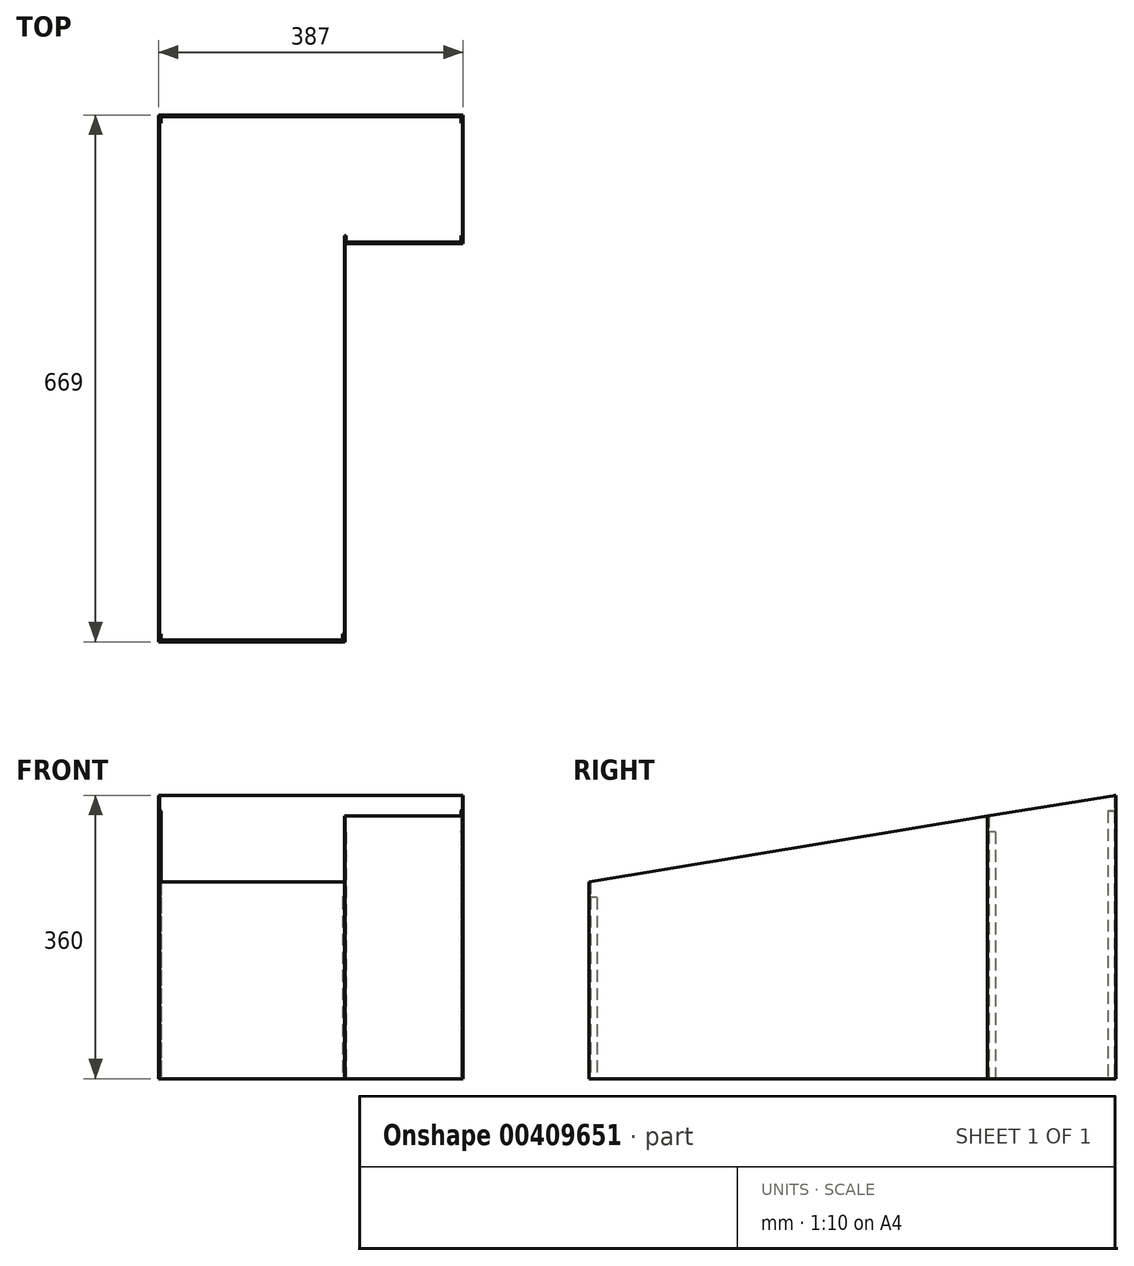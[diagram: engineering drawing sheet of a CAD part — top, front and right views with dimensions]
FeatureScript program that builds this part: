
annotation { "Feature Type Name" : "Feature", "Feature Type Description" : "" }
export const myFeature = defineFeature(function(context is Context, id is Id, definition is map)
    precondition{}
    {
        {
            var Q0;
            Q0=qCreatedBy(makeId("Top.planeOp"),FACE);
            var sketch = newSketch(context, id + "F0", { "sketchPlane" : qUnion([Q0])});
            skLineSegment(sketch, "E0.bottom", {"start": v(192.5, 300) * mm, "end": v(-192.5, 300) * mm});
            skLineSegment(sketch, "E0.top", {"start": v(192.5, 302) * mm, "end": v(-192.5, 302) * mm});
            skLineSegment(sketch, "E0.left", {"start": v(192.5, 300) * mm, "end": v(192.5, 302) * mm});
            skLineSegment(sketch, "E0.right", {"start": v(-192.5, 300) * mm, "end": v(-192.5, 302) * mm});
            skPoint(sketch, "E0.middle", {"position": v(0, 301) * mm});
            skLineSegment(sketch, "E1.bottom", {"start": v(-192.5, 300) * mm, "end": v(-190.5, 300) * mm});
            skLineSegment(sketch, "E1.top", {"start": v(-192.5, 292) * mm, "end": v(-190.5, 292) * mm});
            skLineSegment(sketch, "E1.left", {"start": v(-192.5, 300) * mm, "end": v(-192.5, 292) * mm});
            skLineSegment(sketch, "E1.right", {"start": v(-190.5, 300) * mm, "end": v(-190.5, 292) * mm});
            skLineSegment(sketch, "E2.bottom", {"start": v(192.5, 300) * mm, "end": v(190.5, 300) * mm});
            skLineSegment(sketch, "E2.top", {"start": v(192.5, 292) * mm, "end": v(190.5, 292) * mm});
            skLineSegment(sketch, "E2.left", {"start": v(192.5, 300) * mm, "end": v(192.5, 292) * mm});
            skLineSegment(sketch, "E2.right", {"start": v(190.5, 300) * mm, "end": v(190.5, 292) * mm});
            skSolve(sketch);
        }
        {
            var Q0;
            Q0 = qSketchRegion(id + "F0", true);
            extrude(context, id + "F1", {"entities" : qUnion([Q0]), "depth" : 360 * mm});
        }
        {
            var Q0;
            Q0=qCreatedBy(makeId("Top.planeOp"),FACE);
            var sketch = newSketch(context, id + "F2", { "sketchPlane" : qUnion([Q0])});
            skLineSegment(sketch, "E3.bottom", {"start": v(42.5, -367) * mm, "end": v(-192.5, -367) * mm});
            skLineSegment(sketch, "E3.top", {"start": v(42.5, -365) * mm, "end": v(-192.5, -365) * mm});
            skLineSegment(sketch, "E3.left", {"start": v(42.5, -367) * mm, "end": v(42.5, -365) * mm});
            skLineSegment(sketch, "E3.right", {"start": v(-192.5, -367) * mm, "end": v(-192.5, -365) * mm});
            skPoint(sketch, "E3.middle", {"position": v(-75, -366) * mm});
            skLineSegment(sketch, "E4.bottom", {"start": v(-192.5, -365) * mm, "end": v(-190.5, -365) * mm});
            skLineSegment(sketch, "E4.top", {"start": v(-192.5, -357) * mm, "end": v(-190.5, -357) * mm});
            skLineSegment(sketch, "E4.left", {"start": v(-192.5, -365) * mm, "end": v(-192.5, -357) * mm});
            skLineSegment(sketch, "E4.right", {"start": v(-190.5, -365) * mm, "end": v(-190.5, -357) * mm});
            skLineSegment(sketch, "E5.bottom", {"start": v(42.5, -365) * mm, "end": v(40.5, -365) * mm});
            skLineSegment(sketch, "E5.top", {"start": v(42.5, -357) * mm, "end": v(40.5, -357) * mm});
            skLineSegment(sketch, "E5.left", {"start": v(42.5, -365) * mm, "end": v(42.5, -357) * mm});
            skLineSegment(sketch, "E5.right", {"start": v(40.5, -365) * mm, "end": v(40.5, -357) * mm});
            skSolve(sketch);
        }
        {
            var Q0;
            Q0 = qSketchRegion(id + "F2", true);
            extrude(context, id + "F3", {"entities" : qUnion([Q0]), "depth" : 250 * mm});
        }
        {
            var Q0;
            Q0=qCreatedBy(makeId("Top.planeOp"),FACE);
            var sketch = newSketch(context, id + "F4", { "sketchPlane" : qUnion([Q0])});
            skLineSegment(sketch, "E6.bottom", {"start": v(192.5, 139) * mm, "end": v(42.5, 139) * mm});
            skLineSegment(sketch, "E6.top", {"start": v(192.5, 141) * mm, "end": v(42.5, 141) * mm});
            skLineSegment(sketch, "E6.left", {"start": v(192.5, 139) * mm, "end": v(192.5, 141) * mm});
            skLineSegment(sketch, "E6.right", {"start": v(42.5, 139) * mm, "end": v(42.5, 141) * mm});
            skPoint(sketch, "E6.middle", {"position": v(117.5, 140) * mm});
            skLineSegment(sketch, "E7.bottom", {"start": v(192.5, 141) * mm, "end": v(190.5, 141) * mm});
            skLineSegment(sketch, "E7.top", {"start": v(192.5, 149) * mm, "end": v(190.5, 149) * mm});
            skLineSegment(sketch, "E7.left", {"start": v(192.5, 141) * mm, "end": v(192.5, 149) * mm});
            skLineSegment(sketch, "E7.right", {"start": v(190.5, 141) * mm, "end": v(190.5, 149) * mm});
            skLineSegment(sketch, "E8.bottom", {"start": v(42.5, 141) * mm, "end": v(44.5, 141) * mm});
            skLineSegment(sketch, "E8.top", {"start": v(42.5, 149) * mm, "end": v(44.5, 149) * mm});
            skLineSegment(sketch, "E8.left", {"start": v(42.5, 141) * mm, "end": v(42.5, 149) * mm});
            skLineSegment(sketch, "E8.right", {"start": v(44.5, 141) * mm, "end": v(44.5, 149) * mm});
            skSolve(sketch);
        }
        {
            var Q0;
            Q0 = qSketchRegion(id + "F4", true);
            extrude(context, id + "F5", {"entities" : qUnion([Q0]), "depth" : 333.5 * mm});
        }
        {
            var Q0;
            Q0=qCreatedBy(makeId("Right.planeOp"),FACE);
            var sketch = newSketch(context, id + "F6", { "sketchPlane" : qUnion([Q0])});
            skLineSegment(sketch, "E9", {"start": v(300, 0) * mm, "end": v(-365, 0) * mm});
            skLineSegment(sketch, "E10", {"start": v(-365, 0) * mm, "end": v(-365, 250) * mm});
            skLineSegment(sketch, "E11", {"start": v(-365, 250) * mm, "end": v(300, 360) * mm});
            skLineSegment(sketch, "E12", {"start": v(300, 360) * mm, "end": v(300, 0) * mm});
            skLineSegment(sketch, "E13", {"start": v(139, 333.37) * mm, "end": v(139, 0) * mm});
            skSolve(sketch);
        }
        {
            var Q0;
            Q0=makeQuery(id+"F1.opExtrude","SWEPT_FACE",FACE,{"disambiguationData":[OSD([sQuery(id+"F0.wireOp",EDGE,"E0.right"),sQuery(id+"F0.wireOp",EDGE,"E1.left")])]});
            var sketch = newSketch(context, id + "F7", { "sketchPlane" : qUnion([Q0])});
            skLineSegment(sketch, "E14.bottom", {"start": v(-292, 360) * mm, "end": v(-300, 360) * mm});
            skLineSegment(sketch, "E14.top", {"start": v(-292, 340) * mm, "end": v(-300, 340) * mm});
            skLineSegment(sketch, "E14.left", {"start": v(-292, 360) * mm, "end": v(-292, 340) * mm});
            skLineSegment(sketch, "E14.right", {"start": v(-300, 360) * mm, "end": v(-300, 340) * mm});
            skLineSegment(sketch, "E15.bottom", {"start": v(357, 250) * mm, "end": v(365, 250) * mm});
            skLineSegment(sketch, "E15.top", {"start": v(357, 230) * mm, "end": v(365, 230) * mm});
            skLineSegment(sketch, "E15.left", {"start": v(357, 250) * mm, "end": v(357, 230) * mm});
            skLineSegment(sketch, "E15.right", {"start": v(365, 250) * mm, "end": v(365, 230) * mm});
            skLineSegment(sketch, "E16.bottom", {"start": v(-149, 333.5) * mm, "end": v(-141, 333.5) * mm});
            skLineSegment(sketch, "E16.top", {"start": v(-149, 313.5) * mm, "end": v(-141, 313.5) * mm});
            skLineSegment(sketch, "E16.left", {"start": v(-149, 333.5) * mm, "end": v(-149, 313.5) * mm});
            skLineSegment(sketch, "E16.right", {"start": v(-141, 333.5) * mm, "end": v(-141, 313.5) * mm});
            skSolve(sketch);
        }
        {
            var Q0;
            Q0 = qSketchRegion(id + "F7", true);
            extrude(context, id + "F8", {"entities" : qUnion([Q0]), "operationType" : NewBodyOperationType.REMOVE, "oppositeDirection" : true, "depth" : 385 * mm});
        }
        {
            var Q0;
            Q0=makeQuery(id+"F1.opExtrude","SWEPT_EDGE",EDGE,{"disambiguationData":[OSD([sQuery(id+"F0.wireOp",EDGE,"E0.top"),sQuery(id+"F0.wireOp",EDGE,"E0.right")])]});
            var Q1;
            Q1=makeQuery(id+"F1.opExtrude","SWEPT_EDGE",EDGE,{"disambiguationData":[OSD([sQuery(id+"F0.wireOp",EDGE,"E0.bottom"),sQuery(id+"F0.wireOp",EDGE,"E1.bottom"),sQuery(id+"F0.wireOp",EDGE,"E1.right")])]});
            var Q2;
            Q2=makeQuery(id+"F1.opExtrude","SWEPT_EDGE",EDGE,{"disambiguationData":[OSD([sQuery(id+"F0.wireOp",EDGE,"E0.top"),sQuery(id+"F0.wireOp",EDGE,"E0.left")])]});
            var Q3;
            Q3=makeQuery(id+"F1.opExtrude","SWEPT_EDGE",EDGE,{"disambiguationData":[OSD([sQuery(id+"F0.wireOp",EDGE,"E0.bottom"),sQuery(id+"F0.wireOp",EDGE,"E2.bottom"),sQuery(id+"F0.wireOp",EDGE,"E2.right")])]});
            var Q4;
            Q4=makeQuery(id+"F5.opExtrude","SWEPT_EDGE",EDGE,{"disambiguationData":[OSD([sQuery(id+"F4.wireOp",EDGE,"E6.top"),sQuery(id+"F4.wireOp",EDGE,"E6.right")])]});
            var Q5;
            Q5=makeQuery(id+"F5.opExtrude","SWEPT_EDGE",EDGE,{"disambiguationData":[OSD([sQuery(id+"F4.wireOp",EDGE,"E6.bottom"),sQuery(id+"F4.wireOp",EDGE,"Lwx0521F-HdKg-0JuQ-QpQ8-ElHJVKWACzqa.bottom"),sQuery(id+"F4.wireOp",EDGE,"Lwx0521F-HdKg-0JuQ-QpQ8-ElHJVKWACzqa.right")])]});
            var Q6;
            Q6=makeQuery(id+"F5.opExtrude","SWEPT_EDGE",EDGE,{"disambiguationData":[OSD([sQuery(id+"F4.wireOp",EDGE,"E6.bottom"),sQuery(id+"F4.wireOp",EDGE,"E6.left")])]});
            var Q7;
            Q7=makeQuery(id+"F5.opExtrude","SWEPT_EDGE",EDGE,{"disambiguationData":[OSD([sQuery(id+"F4.wireOp",EDGE,"E6.top"),sQuery(id+"F4.wireOp",EDGE,"E7.bottom"),sQuery(id+"F4.wireOp",EDGE,"E7.right")])]});
            var Q8;
            Q8=makeQuery(id+"F3.opExtrude","SWEPT_EDGE",EDGE,{"disambiguationData":[OSD([sQuery(id+"F2.wireOp",EDGE,"E3.bottom"),sQuery(id+"F2.wireOp",EDGE,"E3.left")])]});
            var Q9;
            Q9=makeQuery(id+"F3.opExtrude","SWEPT_EDGE",EDGE,{"disambiguationData":[OSD([sQuery(id+"F2.wireOp",EDGE,"E3.top"),sQuery(id+"F2.wireOp",EDGE,"E5.bottom"),sQuery(id+"F2.wireOp",EDGE,"E5.right")])]});
            var Q10;
            Q10=makeQuery(id+"F3.opExtrude","SWEPT_EDGE",EDGE,{"disambiguationData":[OSD([sQuery(id+"F2.wireOp",EDGE,"E3.top"),sQuery(id+"F2.wireOp",EDGE,"E4.bottom"),sQuery(id+"F2.wireOp",EDGE,"E4.right")])]});
            var Q11;
            Q11=makeQuery(id+"F3.opExtrude","SWEPT_EDGE",EDGE,{"disambiguationData":[OSD([sQuery(id+"F2.wireOp",EDGE,"E3.bottom"),sQuery(id+"F2.wireOp",EDGE,"E3.right")])]});
            fillet(context, id + "F9", {"entities" : qUnion([Q0, Q1, Q2, Q3, Q4, Q5, Q6, Q7, Q8, Q9, Q10, Q11]), "radius" : 1 * mm, "tangentPropagation" : true, "allowEdgeOverflow" : false});
        }
        {
            var Q0;
            Q0=qCreatedBy(makeId("Right.planeOp"),FACE);
            cPlane(context, id + "F10", {"entities" : qUnion([Q0]), "cplaneType" : CPlaneType.OFFSET, "offset" : 192.5 * mm, "oppositeDirection" : true, "width" : 150 * mm, "height" : 150 * mm});
        }
        {
            var Q0;
            Q0=qCreatedBy(id+"F10.planeOp",FACE);
            var sketch = newSketch(context, id + "F11", { "sketchPlane" : qUnion([Q0])});
            skLineSegment(sketch, "E17", {"start": v(302, 0) * mm, "end": v(-367, 0) * mm});
            skLineSegment(sketch, "E18", {"start": v(-367, 0) * mm, "end": v(-367, 250) * mm});
            skLineSegment(sketch, "E19", {"start": v(-367, 250) * mm, "end": v(302, 360) * mm});
            skLineSegment(sketch, "E20", {"start": v(302, 360) * mm, "end": v(302, 0) * mm});
            skSolve(sketch);
        }
        {
            var Q0;
            Q0 = qSketchRegion(id + "F11", true);
            extrude(context, id + "F12", {"entities" : qUnion([Q0]), "oppositeDirection" : true, "depth" : 1 * mm});
        }
        {
            var Q0;
            Q0=qCreatedBy(makeId("Right.planeOp"),FACE);
            cPlane(context, id + "F13", {"entities" : qUnion([Q0]), "cplaneType" : CPlaneType.OFFSET, "offset" : 192.5 * mm, "width" : 150 * mm, "height" : 150 * mm});
        }
        {
            var Q0;
            Q0=qCreatedBy(id+"F13.planeOp",FACE);
            var sketch = newSketch(context, id + "F14", { "sketchPlane" : qUnion([Q0])});
            skLineSegment(sketch, "E21", {"start": v(302, 0) * mm, "end": v(139, 0) * mm});
            skLineSegment(sketch, "E22", {"start": v(139, 0) * mm, "end": v(139, 333.5) * mm});
            skLineSegment(sketch, "E23", {"start": v(139, 333.5) * mm, "end": v(302, 360) * mm});
            skLineSegment(sketch, "E24", {"start": v(302, 360) * mm, "end": v(302, 0) * mm});
            skSolve(sketch);
        }
        {
            var Q0;
            Q0 = qSketchRegion(id + "F14", true);
            extrude(context, id + "F15", {"entities" : qUnion([Q0]), "depth" : 1 * mm});
        }
        {
            var Q0;
            Q0=qCreatedBy(makeId("Right.planeOp"),FACE);
            cPlane(context, id + "F16", {"entities" : qUnion([Q0]), "cplaneType" : CPlaneType.OFFSET, "offset" : 42.5 * mm, "width" : 150 * mm, "height" : 150 * mm});
        }
        {
            var Q0;
            Q0=qCreatedBy(id+"F16.planeOp",FACE);
            var sketch = newSketch(context, id + "F17", { "sketchPlane" : qUnion([Q0])});
            skLineSegment(sketch, "E25", {"start": v(-367, 250) * mm, "end": v(-367, 0) * mm});
            skLineSegment(sketch, "E26", {"start": v(-367, 0) * mm, "end": v(139, 0) * mm});
            skLineSegment(sketch, "E27", {"start": v(139, 0) * mm, "end": v(139, 333.5) * mm});
            skLineSegment(sketch, "E28", {"start": v(139, 333.5) * mm, "end": v(-367, 250) * mm});
            skSolve(sketch);
        }
        {
            var Q0;
            Q0 = qSketchRegion(id + "F17", true);
            extrude(context, id + "F18", {"entities" : qUnion([Q0]), "depth" : 1 * mm});
        }
    });
